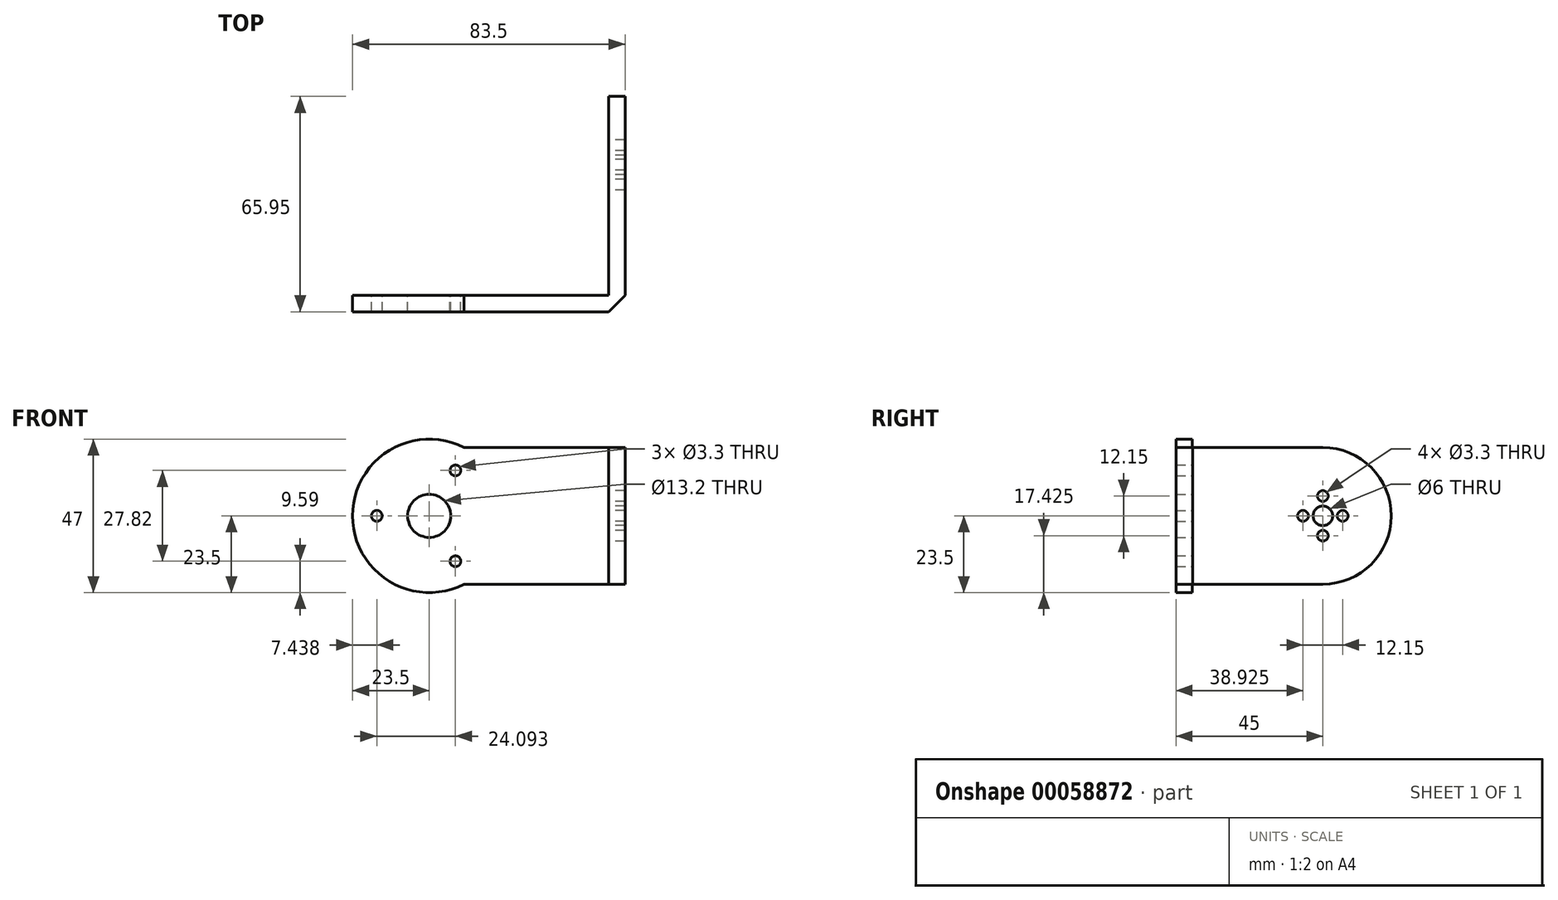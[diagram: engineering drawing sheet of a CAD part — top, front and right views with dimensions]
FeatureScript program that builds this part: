
annotation { "Feature Type Name" : "Feature", "Feature Type Description" : "" }
export const myFeature = defineFeature(function(context is Context, id is Id, definition is map)
    precondition{}
    {
        {
            var Q0;
            Q0=qCreatedBy(makeId("Front.planeOp"),FACE);
            var sketch = newSketch(context, id + "F0", { "sketchPlane" : qUnion([Q0])});
            skCircle(sketch, "E0", {"center": v(0, 0) * mm, "radius": 23.5 * mm});
            skCircle(sketch, "E1", {"center": v(-16.06, 0) * mm, "radius": 1.65 * mm});
            skLineSegment(sketch, "E2", {"start": v(-16.06, 0) * mm, "end": v(0, 0) * mm, "construction": true});
            skLineSegment(sketch, "E3.1.0", {"start": v(8.03, -13.91) * mm, "end": v(0, 0) * mm, "construction": true});
            skCircle(sketch, "E3.1.1", {"center": v(8.03, -13.91) * mm, "radius": 1.65 * mm});
            skLineSegment(sketch, "E3.2.0", {"start": v(8.03, 13.91) * mm, "end": v(0, 0) * mm, "construction": true});
            skCircle(sketch, "E3.2.1", {"center": v(8.03, 13.91) * mm, "radius": 1.65 * mm});
            skCircle(sketch, "E4", {"center": v(0, 0) * mm, "radius": 6.6 * mm});
            skSolve(sketch);
        }
        {
            var Q0;
            Q0 = qSketchRegion(id + "F0", true);
            extrude(context, id + "F1", {"entities" : qUnion([Q0]), "depth" : 5 * mm});
        }
        {
            var Q0;
            Q0=qCreatedBy(makeId("Front.planeOp"),FACE);
            var sketch = newSketch(context, id + "F2", { "sketchPlane" : qUnion([Q0])});
            skLineSegment(sketch, "E5.bottom", {"start": v(10.64, 20.95) * mm, "end": v(60, 20.95) * mm});
            skLineSegment(sketch, "E5.top", {"start": v(10.64, -20.95) * mm, "end": v(60, -20.95) * mm});
            skLineSegment(sketch, "E5.left", {"start": v(10.64, 20.95) * mm, "end": v(10.64, -20.95) * mm});
            skLineSegment(sketch, "E5.right", {"start": v(60, 20.96) * mm, "end": v(60, -20.96) * mm});
            skSolve(sketch);
        }
        {
            var Q0;
            Q0 = qSketchRegion(id + "F2", true);
            extrude(context, id + "F3", {"entities" : qUnion([Q0]), "operationType" : NewBodyOperationType.ADD, "depth" : 5 * mm});
        }
        {
            var Q0;
            Q0=makeQuery(id+"F3.boolean.opBoolean","MERGE",FACE,{"derivedFrom":[makeQuery(id+"F1.opExtrude","CAP_FACE",FACE,{"disambiguationData":[OSD([sQuery(id+"F0.wireOp",EDGE,"E0"),sQuery(id+"F0.wireOp",EDGE,"E1"),sQuery(id+"F0.wireOp",EDGE,"E3.1.1"),sQuery(id+"F0.wireOp",EDGE,"E3.2.1")])],"isStart":true}),makeQuery(id+"F3.opExtrude","CAP_FACE",FACE,{"disambiguationData":[OSD([sQuery(id+"F2.wireOp",EDGE,"E5.bottom"),sQuery(id+"F2.wireOp",EDGE,"E5.top"),sQuery(id+"F2.wireOp",EDGE,"E5.left"),sQuery(id+"F2.wireOp",EDGE,"E5.right")])],"isStart":true})]});
            var sketch = newSketch(context, id + "F4", { "sketchPlane" : qUnion([Q0])});
            skLineSegment(sketch, "E6.bottom", {"start": v(-60, -20.96) * mm, "end": v(-55, -20.96) * mm});
            skLineSegment(sketch, "E6.top", {"start": v(-60, 20.95) * mm, "end": v(-55, 20.95) * mm});
            skLineSegment(sketch, "E6.left", {"start": v(-60, -20.96) * mm, "end": v(-60, 20.95) * mm});
            skLineSegment(sketch, "E6.right", {"start": v(-55, -20.96) * mm, "end": v(-55, 20.95) * mm});
            skSolve(sketch);
        }
        {
            var Q0;
            Q0 = qSketchRegion(id + "F4", true);
            extrude(context, id + "F5", {"entities" : qUnion([Q0]), "operationType" : NewBodyOperationType.ADD, "depth" : 40 * mm});
        }
        {
            var Q0;
            Q0=makeQuery(id+"F5.opExtrude","SWEPT_FACE",FACE,{"disambiguationData":[OSD([sQuery(id+"F4.wireOp",EDGE,"E6.right")])]});
            var sketch = newSketch(context, id + "F6", { "sketchPlane" : qUnion([Q0])});
            skCircle(sketch, "E7", {"center": v(-40, 0) * mm, "radius": 20.95 * mm});
            skSolve(sketch);
        }
        {
            var Q0;
            Q0 = qSketchRegion(id + "F6", true);
            extrude(context, id + "F7", {"entities" : qUnion([Q0]), "operationType" : NewBodyOperationType.ADD, "oppositeDirection" : true, "depth" : 5 * mm});
        }
        {
            var Q0;
            Q0=makeQuery(id+"F7.boolean.opBoolean","MERGE",FACE,{"derivedFrom":[makeQuery(id+"F5.opExtrude","SWEPT_FACE",FACE,{"disambiguationData":[OSD([sQuery(id+"F4.wireOp",EDGE,"E6.right")])]}),makeQuery(id+"F7.opExtrude","CAP_FACE",FACE,{"disambiguationData":[OSD([sQuery(id+"F6.wireOp",EDGE,"E7")])],"isStart":true})]});
            var sketch = newSketch(context, id + "F8", { "sketchPlane" : qUnion([Q0])});
            skLineSegment(sketch, "E8", {"start": v(-60.95, 0) * mm, "end": v(-33.1, 0) * mm, "construction": true});
            skPoint(sketch, "E8.endSnap0", {"position": v(-60.95, 0) * mm});
            skLineSegment(sketch, "E9", {"start": v(-40, 20.96) * mm, "end": v(-40, -20.95) * mm, "construction": true});
            skCircle(sketch, "E10", {"center": v(-40, 6.08) * mm, "radius": 1.65 * mm});
            skPoint(sketch, "E11", {"position": v(-40, 0) * mm});
            skCircle(sketch, "E12.1.0", {"center": v(-46.07, 0) * mm, "radius": 1.65 * mm});
            skCircle(sketch, "E12.2.0", {"center": v(-40, -6.07) * mm, "radius": 1.65 * mm});
            skCircle(sketch, "E12.3.0", {"center": v(-33.93, 0) * mm, "radius": 1.65 * mm});
            skCircle(sketch, "E13", {"center": v(-40, 0) * mm, "radius": 3 * mm});
            skSolve(sketch);
        }
        {
            var Q0;
            Q0 = qSketchRegion(id + "F8", true);
            extrude(context, id + "F9", {"entities" : qUnion([Q0]), "operationType" : NewBodyOperationType.REMOVE, "oppositeDirection" : true, "depth" : 25.4 * mm});
        }
        {
            var Q0;
            Q0=makeQuery(id+"F5.opExtrude","CAP_EDGE",EDGE,{"disambiguationData":[OSD([sQuery(id+"F4.wireOp",EDGE,"E6.right")])],"isStart":true});
            var Q1;
            Q1=makeQuery(id+"F3.opExtrude","CAP_EDGE",EDGE,{"disambiguationData":[OSD([sQuery(id+"F2.wireOp",EDGE,"E5.right")])],"isStart":false});
            chamfer(context, id + "F10", {"entities" : qUnion([Q0, Q1]), "width" : 5.08 * mm, "tangentPropagation" : true});
        }
    });
